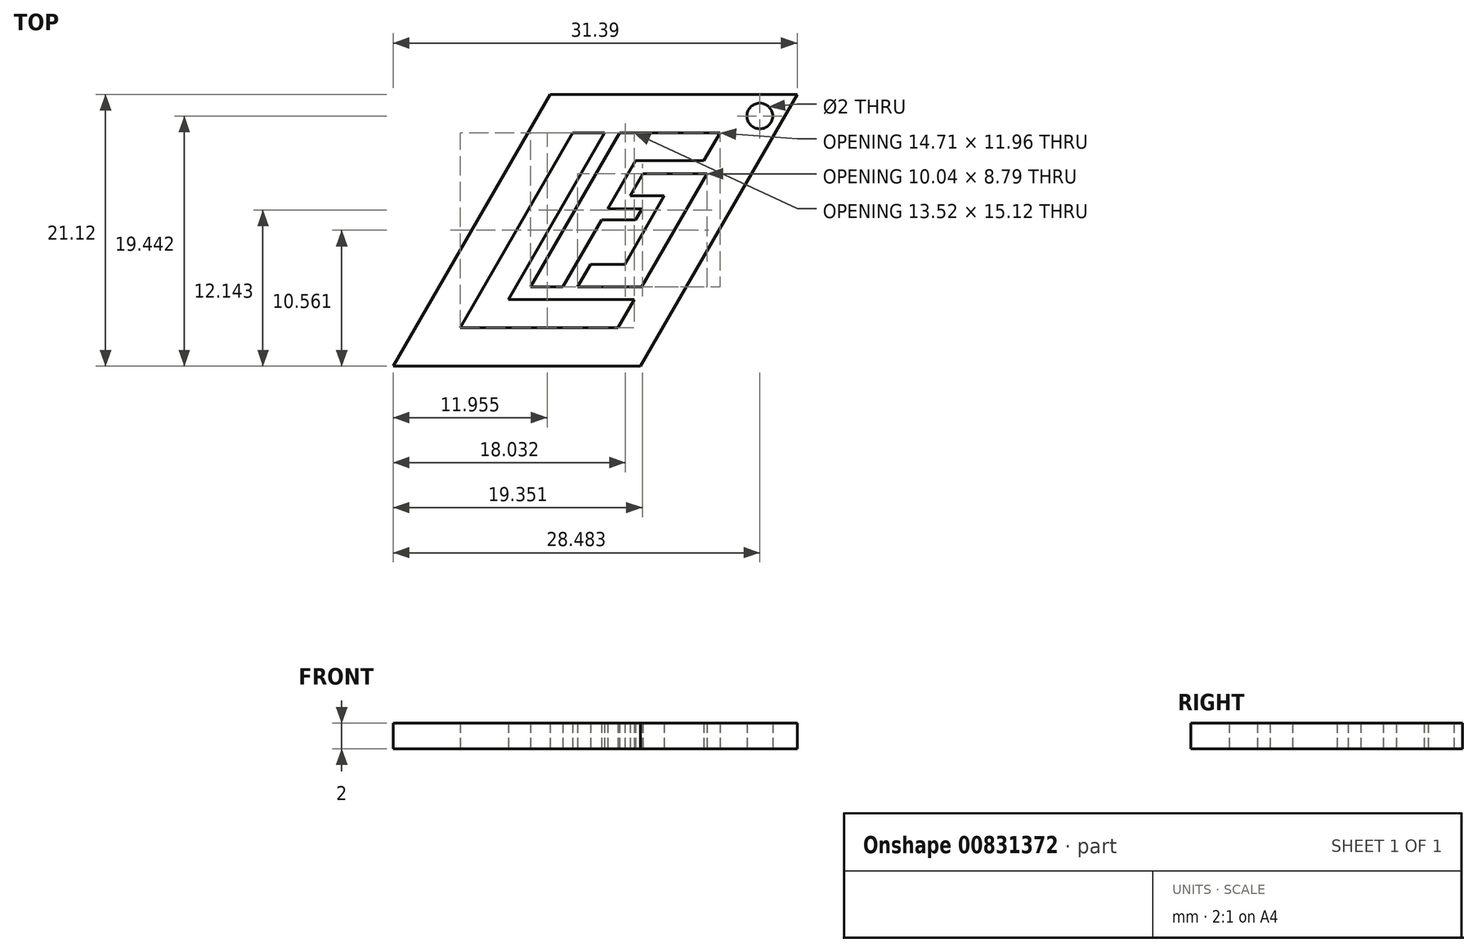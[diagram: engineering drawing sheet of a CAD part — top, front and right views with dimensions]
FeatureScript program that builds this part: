
annotation { "Feature Type Name" : "Feature", "Feature Type Description" : "" }
export const myFeature = defineFeature(function(context is Context, id is Id, definition is map)
    precondition{}
    {
        {
            var Q0;
            Q0=qCreatedBy(makeId("Top.planeOp"),FACE);
            var sketch = newSketch(context, id + "F0", { "sketchPlane" : qUnion([Q0])});
            skLineSegment(sketch, "E0", {"start": v(-8.15, -5.2) * mm, "end": v(-5.65, -5.2) * mm});
            skLineSegment(sketch, "E1", {"start": v(-5.65, -5.2) * mm, "end": v(-2.65, 0) * mm});
            skLineSegment(sketch, "E2", {"start": v(-2.65, 0) * mm, "end": v(0, 0) * mm});
            skLineSegment(sketch, "E3", {"start": v(0, 0) * mm, "end": v(0.5, 0.87) * mm});
            skLineSegment(sketch, "E4", {"start": v(0.5, 0.87) * mm, "end": v(-2.15, 0.87) * mm});
            skLineSegment(sketch, "E5", {"start": v(-2.15, 0.87) * mm, "end": v(0, 4.6) * mm});
            skLineSegment(sketch, "E6", {"start": v(0, 4.6) * mm, "end": v(2.65, 4.6) * mm});
            skLineSegment(sketch, "E7", {"start": v(5.3, 4.6) * mm, "end": v(6.56, 6.76) * mm});
            skLineSegment(sketch, "E8", {"start": v(6.56, 6.76) * mm, "end": v(-1.25, 6.76) * mm});
            skLineSegment(sketch, "E9", {"start": v(-1.25, 6.76) * mm, "end": v(-8.15, -5.2) * mm});
            skLineSegment(sketch, "E10", {"start": v(2.65, 4.6) * mm, "end": v(5.3, 4.6) * mm});
            skLineSegment(sketch, "E11", {"start": v(2.65, 4.6) * mm, "end": v(0.5, 0.87) * mm, "construction": true});
            skCircle(sketch, "E12", {"center": v(-0.78, 5.95) * mm, "radius": 0.5 * mm});
            skLineSegment(sketch, "E13", {"start": v(-1.25, 6.76) * mm, "end": v(-0.94, 6.22) * mm, "construction": true});
            skLineSegment(sketch, "E14", {"start": v(-0.31, 5.14) * mm, "end": v(0, 4.6) * mm, "construction": true});
            skLineSegment(sketch, "E15", {"start": v(-0.94, 6.22) * mm, "end": v(-0.62, 5.68) * mm, "construction": true});
            skLineSegment(sketch, "E16", {"start": v(-0.62, 5.68) * mm, "end": v(-0.31, 5.14) * mm, "construction": true});
            skLineSegment(sketch, "E17", {"start": v(-2.4, 6.76) * mm, "end": v(-9.89, -6.2) * mm});
            skLineSegment(sketch, "E18", {"start": v(-9.89, -6.2) * mm, "end": v(-0.11, -6.2) * mm});
            skLineSegment(sketch, "E19", {"start": v(-0.11, -6.2) * mm, "end": v(-1.36, -8.36) * mm});
            skLineSegment(sketch, "E20", {"start": v(-1.36, -8.36) * mm, "end": v(-13.64, -8.36) * mm});
            skLineSegment(sketch, "E21", {"start": v(-13.64, -8.36) * mm, "end": v(-4.9, 6.76) * mm});
            skLineSegment(sketch, "E22", {"start": v(-4.9, 6.76) * mm, "end": v(-2.4, 6.76) * mm});
            skLineSegment(sketch, "E23", {"start": v(-3.5, -3.46) * mm, "end": v(-4.5, -5.2) * mm});
            skLineSegment(sketch, "E24", {"start": v(-4.5, -5.2) * mm, "end": v(0.46, -5.2) * mm});
            skLineSegment(sketch, "E25", {"start": v(0.46, -5.2) * mm, "end": v(5.54, 3.6) * mm});
            skLineSegment(sketch, "E26", {"start": v(5.54, 3.6) * mm, "end": v(0.58, 3.6) * mm});
            skLineSegment(sketch, "E27", {"start": v(0.58, 3.6) * mm, "end": v(-0.42, 1.87) * mm});
            skLineSegment(sketch, "E28", {"start": v(-0.42, 1.87) * mm, "end": v(2.23, 1.87) * mm});
            skLineSegment(sketch, "E29", {"start": v(2.23, 1.87) * mm, "end": v(-0.85, -3.46) * mm});
            skLineSegment(sketch, "E30", {"start": v(-0.85, -3.46) * mm, "end": v(-3.5, -3.46) * mm});
            skLineSegment(sketch, "E31", {"start": v(12.56, 9.76) * mm, "end": v(-6.64, 9.76) * mm});
            skLineSegment(sketch, "E32", {"start": v(-6.64, 9.76) * mm, "end": v(-18.83, -11.36) * mm});
            skLineSegment(sketch, "E33", {"start": v(-18.83, -11.36) * mm, "end": v(0.37, -11.36) * mm});
            skLineSegment(sketch, "E34", {"start": v(0.37, -11.36) * mm, "end": v(12.56, 9.76) * mm});
            skCircle(sketch, "E35", {"center": v(9.65, 8.08) * mm, "radius": 1 * mm});
            skLineSegment(sketch, "E36", {"start": v(-18.83, -11.36) * mm, "end": v(12.56, 9.76) * mm, "construction": true});
            skLineSegment(sketch, "E37", {"start": v(12.56, 9.76) * mm, "end": v(9.65, 8.08) * mm, "construction": true});
            skLineSegment(sketch, "E38", {"start": v(11.1, 7.24) * mm, "end": v(9.65, 8.08) * mm, "construction": true});
            skLineSegment(sketch, "E39", {"start": v(9.65, 8.08) * mm, "end": v(9.65, 9.76) * mm, "construction": true});
            skLineSegment(sketch, "E40", {"start": v(9.65, 8.08) * mm, "end": v(6.56, 6.76) * mm, "construction": true});
            skSolve(sketch);
        }
        {
            var Q0;
            Q0=makeQuery(id+"F0.imprint","IMPRINT",FACE,{"disambiguationData":[TD([[makeQuery(id+"F0.imprint","IMPRINT",EDGE,{"derivedFrom":sQuery(id+"F0.wireOp",EDGE,"E0")}),-1.0]])]});
            extrude(context, id + "F1", {"entities" : qUnion([Q0]), "depth" : 2 * mm, "offsetDistance" : 25 * mm});
        }
    });
